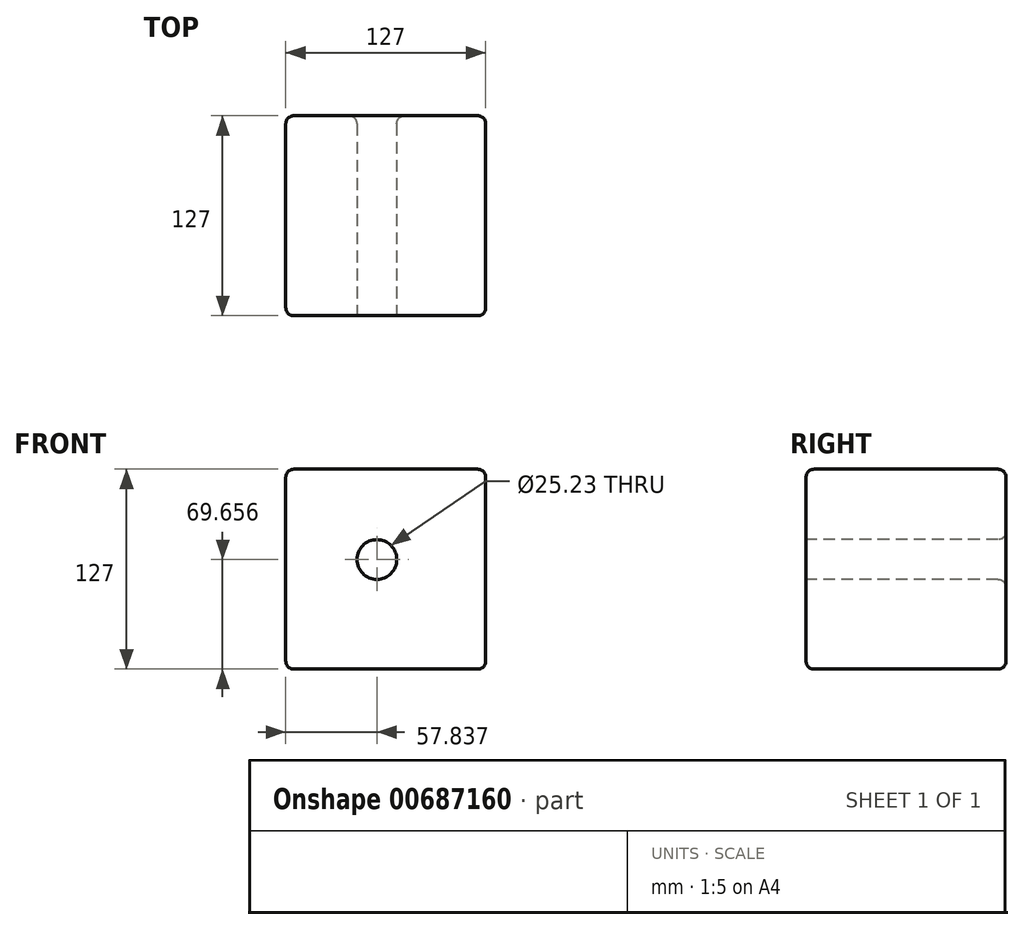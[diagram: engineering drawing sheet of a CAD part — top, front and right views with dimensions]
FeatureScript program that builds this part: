
annotation { "Feature Type Name" : "Feature", "Feature Type Description" : "" }
export const myFeature = defineFeature(function(context is Context, id is Id, definition is map)
    precondition{}
    {
        {
            var Q0;
            Q0=qCreatedBy(makeId("Top.planeOp"),FACE);
            var sketch = newSketch(context, id + "F0", { "sketchPlane" : qUnion([Q0])});
            skLineSegment(sketch, "E0.bottom", {"start": v(0, 0) * mm, "end": v(127, 0) * mm});
            skLineSegment(sketch, "E0.top", {"start": v(0, -127) * mm, "end": v(127, -127) * mm});
            skLineSegment(sketch, "E0.left", {"start": v(0, 0) * mm, "end": v(0, -127) * mm});
            skLineSegment(sketch, "E0.right", {"start": v(127, 0) * mm, "end": v(127, -127) * mm});
            skSolve(sketch);
        }
        {
            var Q0;
            Q0=makeQuery(id+"F0.imprint","IMPRINT",FACE,{"disambiguationData":[TD([[makeQuery(id+"F0.imprint","IMPRINT",EDGE,{"derivedFrom":sQuery(id+"F0.wireOp",EDGE,"E0.bottom")}),-1.0]])]});
            extrude(context, id + "F1", {"entities" : qUnion([Q0]), "depth" : 127 * mm, "offsetDistance" : 25.4 * mm});
        }
        {
            var Q0;
            Q0=makeQuery(id+"F1.opExtrude","CAP_EDGE",EDGE,{"disambiguationData":[OSD([sQuery(id+"F0.wireOp",EDGE,"E0.top")])],"isStart":false});
            var Q1;
            Q1=makeQuery(id+"F1.opExtrude","CAP_EDGE",EDGE,{"disambiguationData":[OSD([sQuery(id+"F0.wireOp",EDGE,"E0.right")])],"isStart":false});
            var Q2;
            Q2=makeQuery(id+"F1.opExtrude","CAP_EDGE",EDGE,{"disambiguationData":[OSD([sQuery(id+"F0.wireOp",EDGE,"E0.left")])],"isStart":false});
            var Q3;
            Q3=makeQuery(id+"F1.opExtrude","CAP_EDGE",EDGE,{"disambiguationData":[OSD([sQuery(id+"F0.wireOp",EDGE,"E0.bottom")])],"isStart":false});
            var Q4;
            Q4=makeQuery(id+"F1.opExtrude","SWEPT_EDGE",EDGE,{"disambiguationData":[OSD([sQuery(id+"F0.wireOp",EDGE,"E0.top"),sQuery(id+"F0.wireOp",EDGE,"E0.right")])]});
            var Q5;
            Q5=makeQuery(id+"F1.opExtrude","CAP_EDGE",EDGE,{"disambiguationData":[OSD([sQuery(id+"F0.wireOp",EDGE,"E0.top")])],"isStart":true});
            var Q6;
            Q6=makeQuery(id+"F1.opExtrude","CAP_EDGE",EDGE,{"disambiguationData":[OSD([sQuery(id+"F0.wireOp",EDGE,"E0.right")])],"isStart":true});
            var Q7;
            Q7=makeQuery(id+"F1.opExtrude","SWEPT_EDGE",EDGE,{"disambiguationData":[OSD([sQuery(id+"F0.wireOp",EDGE,"E0.bottom"),sQuery(id+"F0.wireOp",EDGE,"E0.right")])]});
            var Q8;
            Q8=makeQuery(id+"F1.opExtrude","CAP_EDGE",EDGE,{"disambiguationData":[OSD([sQuery(id+"F0.wireOp",EDGE,"E0.bottom")])],"isStart":true});
            var Q9;
            Q9=makeQuery(id+"F1.opExtrude","SWEPT_EDGE",EDGE,{"disambiguationData":[OSD([sQuery(id+"F0.wireOp",EDGE,"E0.bottom"),sQuery(id+"F0.wireOp",EDGE,"E0.left")])]});
            var Q10;
            Q10=makeQuery(id+"F1.opExtrude","CAP_EDGE",EDGE,{"disambiguationData":[OSD([sQuery(id+"F0.wireOp",EDGE,"E0.left")])],"isStart":true});
            var Q11;
            Q11=makeQuery(id+"F1.opExtrude","SWEPT_EDGE",EDGE,{"disambiguationData":[OSD([sQuery(id+"F0.wireOp",EDGE,"E0.top"),sQuery(id+"F0.wireOp",EDGE,"E0.left")])]});
            fillet(context, id + "F2", {"entities" : qUnion([Q0, Q1, Q2, Q3, Q4, Q5, Q6, Q7, Q8, Q9, Q10, Q11]), "radius" : 5.08 * mm, "tangentPropagation" : true, "allowEdgeOverflow" : false});
        }
        {
            var Q0;
            Q0=makeQuery(id+"F1.opExtrude","SWEPT_FACE",FACE,{"disambiguationData":[OSD([sQuery(id+"F0.wireOp",EDGE,"E0.top")])]});
            var sketch = newSketch(context, id + "F3", { "sketchPlane" : qUnion([Q0])});
            skCircle(sketch, "E1", {"center": v(57.84, 69.66) * mm, "radius": 12.62 * mm});
            skSolve(sketch);
        }
        {
            var Q0;
            Q0 = qSketchRegion(id + "F3", true);
            extrude(context, id + "F4", {"entities" : qUnion([Q0]), "operationType" : NewBodyOperationType.REMOVE, "endBound" : BoundingType.THROUGH_ALL, "oppositeDirection" : true, "depth" : 25.4 * mm, "offsetDistance" : 25.4 * mm});
        }
        {
            var Q0;
            Q0=makeQuery(id+"F4.boolean.opBoolean","COPY",EDGE,{"derivedFrom":makeQuery(id+"F4.opExtrude","CAP_EDGE",EDGE,{"disambiguationData":[OSD([sQuery(id+"F3.wireOp",EDGE,"E1")])],"isStart":true})});
            var Q1;
            Q1=makeQuery(id+"F4.boolean.opBoolean","INTERSECT",EDGE,{"derivedFrom":[makeQuery(id+"F1.opExtrude","SWEPT_FACE",FACE,{"disambiguationData":[OSD([sQuery(id+"F0.wireOp",EDGE,"E0.bottom")])]}),makeQuery(id+"F4.opExtrude","SWEPT_FACE",FACE,{"disambiguationData":[OSD([sQuery(id+"F3.wireOp",EDGE,"E1")])]})]});
            fillet(context, id + "F5", {"entities" : qUnion([Q0, Q1]), "radius" : 5.08 * mm, "tangentPropagation" : true, "allowEdgeOverflow" : false});
        }
    });
